# Revit family: Sensor_Faucet-Zurn-Z6920-XL
name_source: partatom
category: Plumbing Fixtures
units: mm (PartAtom-declared; Revit-internal decimal feet)

## family parameters
Cut with Voids When Loaded = No
Host = Face
Maintain Annotation Orientation = No
OmniClass Number = 23.45.55.14
OmniClass Title = Single Faucets
Part Type = Normal
Room Calculation Point = No
Round Connector Dimension = Use Radius
Shared = No

## types (7) — shared parameters
ADA Compliant = Yes
Activation Method = Sensor Operated
Assembly Code = D2010.60
CW Connection = Yes
CWFU = 1
Description = AquaSense® Gooseneck Sensor Faucet
HW Connection = Yes
HWFU = 1
Height = 10.75 "
Inlet Connection Dimension (in) = 0.5 "
Main Material = Finishes - Zurn - Chromed Plated Brass
Manufacturer = Zurn Water, LLC
Manufacturer Brand = Zurn
Max Working Water Temperature = 140 °F
Model = Z6920-XL
Modified Date = 01/13/2026
Operating Water Pressure Range(Psi) = 10-125PSI
Product Documentation Link = https://files.zurn.com
Product Installation Sheet URL = https://files.zurn.com
Product Page URL = https://www.zurn.com
Product data URL = https://www.bimobject.com
Repair Parts URL = https://files.zurn.com
URL = www.zurn.com
Vent Connection = No
Waste Connection = No
zero-valued in all types: Default Elevation, WFU

## per-type parameters (varying)
| type | Flow Rate (Gpm) | Type of Flow |
| Z6920-XL-F (0.5 GPM Spray Outlet) | 1 GPM | Spray |
| Z6920-XL-E (1.5 GPM Aerator Outlet) | 2 GPM | Aerator |
| Z6920-XL-J (1.5 GPM Laminar Outlet) | 2 GPM | Laminar |
| Z6920-XL-K (1.0 GPM Laminar Outlet) | 1 GPM | Laminar |
| Z6920-XL-L (1.0 Aerator Outlet) | 1 GPM | Aerator |
| Z6920-XL-M (0.35 GPM Spray Outlet) | 0 GPM | Spray |
| Z6920-XL-N  (0.5 GPM Laminar Outlet) | 1 GPM | Laminar |

## geometry (parser evidence)
native form markers: Blend x6, Sweep x20
no freeform markers — native parametric forms only
